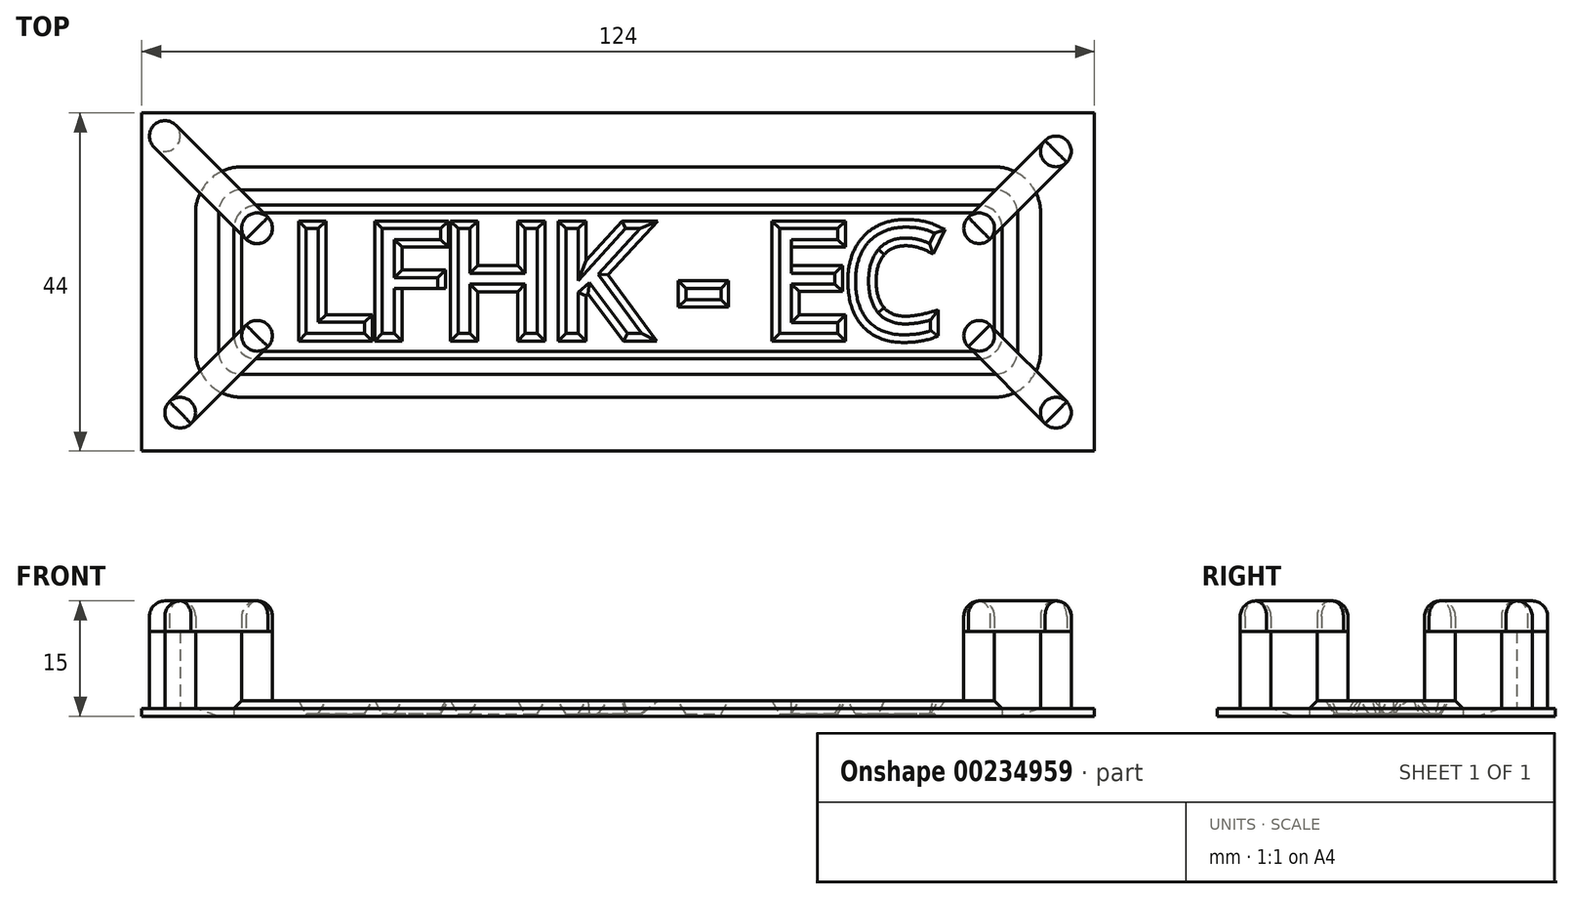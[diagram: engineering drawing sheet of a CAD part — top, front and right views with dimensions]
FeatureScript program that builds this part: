
annotation { "Feature Type Name" : "Feature", "Feature Type Description" : "" }
export const myFeature = defineFeature(function(context is Context, id is Id, definition is map)
    precondition{}
    {
        {
            var Q0;
            Q0=qCreatedBy(makeId("Top.planeOp"),FACE);
            var sketch = newSketch(context, id + "F0", { "sketchPlane" : qUnion([Q0])});
            skLineSegment(sketch, "E0", {"start": v(-50, 3) * mm, "end": v(-50, 17) * mm});
            skLineSegment(sketch, "E1", {"start": v(-47, 20) * mm, "end": v(47, 20) * mm});
            skLineSegment(sketch, "E2", {"start": v(50, 17) * mm, "end": v(50, 3) * mm});
            skLineSegment(sketch, "E3", {"start": v(47, 0) * mm, "end": v(-47, 0) * mm});
            skText(sketch, "E4", { "text": "LFHK - EC", "fontName": "OpenSans-Regular.ttf"});
            skPoint(sketch, "E5.visualSharp", {"position": v(-50, 20) * mm});
            skArc(sketch, "E5.filletArc", {"start": v(-47, 20) * mm, "mid": v(-49.12, 19.12) * mm, "end": v(-50, 17) * mm});
            skPoint(sketch, "E6.visualSharp", {"position": v(-50, 0) * mm});
            skArc(sketch, "E6.filletArc", {"start": v(-50, 3) * mm, "mid": v(-49.12, 0.88) * mm, "end": v(-47, 0) * mm});
            skPoint(sketch, "E7.visualSharp", {"position": v(50, 0) * mm});
            skArc(sketch, "E7.filletArc", {"start": v(47, 0) * mm, "mid": v(49.12, 0.88) * mm, "end": v(50, 3) * mm});
            skPoint(sketch, "E8.visualSharp", {"position": v(50, 20) * mm});
            skArc(sketch, "E8.filletArc", {"start": v(50, 17) * mm, "mid": v(49.12, 19.12) * mm, "end": v(47, 20) * mm});
            const initialGuessF0  = {"E4": [-0.04247, 0.00333, 1, 0, 0.01374]};
            skSetInitialGuess(sketch, initialGuessF0);
            skSolve(sketch);
        }
        {
            var Q0;
            Q0=makeQuery(id+"F0.imprint","IMPRINT",FACE,{"disambiguationData":[TD([[makeQuery(id+"F0.imprint","IMPRINT",EDGE,{"derivedFrom":sQuery(id+"F0.wireOp",EDGE,"E0")}),-1.0]])]});
            extrude(context, id + "F1", {"entities" : qUnion([Q0]), "depth" : 2 * mm});
        }
        {
            var Q0;
            Q0=makeQuery(id+"F1.opExtrude","CAP_EDGE",EDGE,{"disambiguationData":[OSD([sQuery(id+"F0.wireOp",EDGE,"E3")])],"isStart":false});
            var Q1;
            Q1=makeQuery(id+"F1.opExtrude","CAP_EDGE",EDGE,{"disambiguationData":[OSD([sQuery(id+"F0.wireOp",EDGE,"E0")])],"isStart":false});
            var Q2;
            Q2=makeQuery(id+"F1.opExtrude","CAP_EDGE",EDGE,{"disambiguationData":[OSD([sQuery(id+"F0.wireOp",EDGE,"E1")])],"isStart":false});
            var Q3;
            Q3=makeQuery(id+"F1.opExtrude","CAP_EDGE",EDGE,{"disambiguationData":[OSD([sQuery(id+"F0.wireOp",EDGE,"E2")])],"isStart":false});
            chamfer(context, id + "F2", {"entities" : qUnion([Q0, Q1, Q2, Q3]), "chamferType" : ChamferType.OFFSET_ANGLE, "width" : 1 * mm, "oppositeDirection" : false, "angle" : 45 * degree, "tangentPropagation" : true});
        }
        {
            var Q0;
            Q0=makeQuery(id+"F1.opExtrude","CAP_EDGE",EDGE,{"disambiguationData":[OSD([sQuery(id+"F0.wireOp",EDGE,"E4.sketch_text.stroke-1")])],"isStart":false});
            var Q1;
            Q1=makeQuery(id+"F1.opExtrude","CAP_EDGE",EDGE,{"disambiguationData":[OSD([sQuery(id+"F0.wireOp",EDGE,"E4.sketch_text.stroke-3")])],"isStart":false});
            var Q2;
            Q2=makeQuery(id+"F1.opExtrude","CAP_EDGE",EDGE,{"disambiguationData":[OSD([sQuery(id+"F0.wireOp",EDGE,"E4.sketch_text.stroke-2")])],"isStart":false});
            var Q3;
            Q3=makeQuery(id+"F1.opExtrude","CAP_EDGE",EDGE,{"disambiguationData":[OSD([sQuery(id+"F0.wireOp",EDGE,"E4.sketch_text.stroke-0")])],"isStart":false});
            var Q4;
            Q4=makeQuery(id+"F1.opExtrude","CAP_EDGE",EDGE,{"disambiguationData":[OSD([sQuery(id+"F0.wireOp",EDGE,"E4.sketch_text.stroke-5")])],"isStart":false});
            var Q5;
            Q5=makeQuery(id+"F1.opExtrude","CAP_EDGE",EDGE,{"disambiguationData":[OSD([sQuery(id+"F0.wireOp",EDGE,"E4.sketch_text.stroke-4")])],"isStart":false});
            var Q6;
            Q6=makeQuery(id+"F1.opExtrude","CAP_EDGE",EDGE,{"disambiguationData":[OSD([sQuery(id+"F0.wireOp",EDGE,"E4.sketch_text.stroke-13")])],"isStart":false});
            var Q7;
            Q7=makeQuery(id+"F1.opExtrude","CAP_EDGE",EDGE,{"disambiguationData":[OSD([sQuery(id+"F0.wireOp",EDGE,"E4.sketch_text.stroke-9")])],"isStart":false});
            var Q8;
            Q8=makeQuery(id+"F1.opExtrude","CAP_EDGE",EDGE,{"disambiguationData":[OSD([sQuery(id+"F0.wireOp",EDGE,"E4.sketch_text.stroke-8")])],"isStart":false});
            var Q9;
            Q9=makeQuery(id+"F1.opExtrude","CAP_EDGE",EDGE,{"disambiguationData":[OSD([sQuery(id+"F0.wireOp",EDGE,"E4.sketch_text.stroke-10")])],"isStart":false});
            var Q10;
            Q10=makeQuery(id+"F1.opExtrude","CAP_EDGE",EDGE,{"disambiguationData":[OSD([sQuery(id+"F0.wireOp",EDGE,"E4.sketch_text.stroke-12")])],"isStart":false});
            var Q11;
            Q11=makeQuery(id+"F1.opExtrude","CAP_EDGE",EDGE,{"disambiguationData":[OSD([sQuery(id+"F0.wireOp",EDGE,"E4.sketch_text.stroke-11")])],"isStart":false});
            var Q12;
            Q12=makeQuery(id+"F1.opExtrude","CAP_EDGE",EDGE,{"disambiguationData":[OSD([sQuery(id+"F0.wireOp",EDGE,"E4.sketch_text.stroke-7")])],"isStart":false});
            var Q13;
            Q13=makeQuery(id+"F1.opExtrude","CAP_EDGE",EDGE,{"disambiguationData":[OSD([sQuery(id+"F0.wireOp",EDGE,"E4.sketch_text.stroke-15")])],"isStart":false});
            var Q14;
            Q14=makeQuery(id+"F1.opExtrude","CAP_EDGE",EDGE,{"disambiguationData":[OSD([sQuery(id+"F0.wireOp",EDGE,"E4.sketch_text.stroke-6")])],"isStart":false});
            var Q15;
            Q15=makeQuery(id+"F1.opExtrude","CAP_EDGE",EDGE,{"disambiguationData":[OSD([sQuery(id+"F0.wireOp",EDGE,"E4.sketch_text.stroke-21")])],"isStart":false});
            var Q16;
            Q16=makeQuery(id+"F1.opExtrude","CAP_EDGE",EDGE,{"disambiguationData":[OSD([sQuery(id+"F0.wireOp",EDGE,"E4.sketch_text.stroke-22")])],"isStart":false});
            var Q17;
            Q17=makeQuery(id+"F1.opExtrude","CAP_EDGE",EDGE,{"disambiguationData":[OSD([sQuery(id+"F0.wireOp",EDGE,"E4.sketch_text.stroke-23")])],"isStart":false});
            var Q18;
            Q18=makeQuery(id+"F1.opExtrude","CAP_EDGE",EDGE,{"disambiguationData":[OSD([sQuery(id+"F0.wireOp",EDGE,"E4.sketch_text.stroke-26")])],"isStart":false});
            var Q19;
            Q19=makeQuery(id+"F1.opExtrude","CAP_EDGE",EDGE,{"disambiguationData":[OSD([sQuery(id+"F0.wireOp",EDGE,"E4.sketch_text.stroke-25")])],"isStart":false});
            var Q20;
            Q20=makeQuery(id+"F1.opExtrude","CAP_EDGE",EDGE,{"disambiguationData":[OSD([sQuery(id+"F0.wireOp",EDGE,"E4.sketch_text.stroke-24")])],"isStart":false});
            var Q21;
            Q21=makeQuery(id+"F1.opExtrude","CAP_EDGE",EDGE,{"disambiguationData":[OSD([sQuery(id+"F0.wireOp",EDGE,"E4.sketch_text.stroke-18")])],"isStart":false});
            var Q22;
            Q22=makeQuery(id+"F1.opExtrude","CAP_EDGE",EDGE,{"disambiguationData":[OSD([sQuery(id+"F0.wireOp",EDGE,"E4.sketch_text.stroke-19")])],"isStart":false});
            var Q23;
            Q23=makeQuery(id+"F1.opExtrude","CAP_EDGE",EDGE,{"disambiguationData":[OSD([sQuery(id+"F0.wireOp",EDGE,"E4.sketch_text.stroke-20")])],"isStart":false});
            var Q24;
            Q24=makeQuery(id+"F1.opExtrude","CAP_EDGE",EDGE,{"disambiguationData":[OSD([sQuery(id+"F0.wireOp",EDGE,"E4.sketch_text.stroke-16")])],"isStart":false});
            var Q25;
            Q25=makeQuery(id+"F1.opExtrude","CAP_EDGE",EDGE,{"disambiguationData":[OSD([sQuery(id+"F0.wireOp",EDGE,"E4.sketch_text.stroke-17")])],"isStart":false});
            var Q26;
            Q26=makeQuery(id+"F1.opExtrude","CAP_EDGE",EDGE,{"disambiguationData":[OSD([sQuery(id+"F0.wireOp",EDGE,"E4.sketch_text.stroke-27")])],"isStart":false});
            var Q27;
            Q27=makeQuery(id+"F1.opExtrude","CAP_EDGE",EDGE,{"disambiguationData":[OSD([sQuery(id+"F0.wireOp",EDGE,"E4.sketch_text.stroke-33")])],"isStart":false});
            var Q28;
            Q28=makeQuery(id+"F1.opExtrude","CAP_EDGE",EDGE,{"disambiguationData":[OSD([sQuery(id+"F0.wireOp",EDGE,"E4.sketch_text.stroke-34")])],"isStart":false});
            var Q29;
            Q29=makeQuery(id+"F1.opExtrude","CAP_EDGE",EDGE,{"disambiguationData":[OSD([sQuery(id+"F0.wireOp",EDGE,"E4.sketch_text.stroke-35")])],"isStart":false});
            var Q30;
            Q30=makeQuery(id+"F1.opExtrude","CAP_EDGE",EDGE,{"disambiguationData":[OSD([sQuery(id+"F0.wireOp",EDGE,"E4.sketch_text.stroke-30")])],"isStart":false});
            var Q31;
            Q31=makeQuery(id+"F1.opExtrude","CAP_EDGE",EDGE,{"disambiguationData":[OSD([sQuery(id+"F0.wireOp",EDGE,"E4.sketch_text.stroke-36")])],"isStart":false});
            var Q32;
            Q32=makeQuery(id+"F1.opExtrude","CAP_EDGE",EDGE,{"disambiguationData":[OSD([sQuery(id+"F0.wireOp",EDGE,"E4.sketch_text.stroke-31")])],"isStart":false});
            var Q33;
            Q33=makeQuery(id+"F1.opExtrude","CAP_EDGE",EDGE,{"disambiguationData":[OSD([sQuery(id+"F0.wireOp",EDGE,"E4.sketch_text.stroke-32")])],"isStart":false});
            var Q34;
            Q34=makeQuery(id+"F1.opExtrude","CAP_EDGE",EDGE,{"disambiguationData":[OSD([sQuery(id+"F0.wireOp",EDGE,"E4.sketch_text.stroke-37")])],"isStart":false});
            var Q35;
            Q35=makeQuery(id+"F1.opExtrude","CAP_EDGE",EDGE,{"disambiguationData":[OSD([sQuery(id+"F0.wireOp",EDGE,"E4.sketch_text.stroke-38")])],"isStart":false});
            var Q36;
            Q36=makeQuery(id+"F1.opExtrude","CAP_EDGE",EDGE,{"disambiguationData":[OSD([sQuery(id+"F0.wireOp",EDGE,"E4.sketch_text.stroke-39")])],"isStart":false});
            var Q37;
            Q37=makeQuery(id+"F1.opExtrude","CAP_EDGE",EDGE,{"disambiguationData":[OSD([sQuery(id+"F0.wireOp",EDGE,"E4.sketch_text.stroke-29")])],"isStart":false});
            var Q38;
            Q38=makeQuery(id+"F1.opExtrude","CAP_EDGE",EDGE,{"disambiguationData":[OSD([sQuery(id+"F0.wireOp",EDGE,"E4.sketch_text.stroke-28")])],"isStart":false});
            var Q39;
            Q39=makeQuery(id+"F1.opExtrude","CAP_EDGE",EDGE,{"disambiguationData":[OSD([sQuery(id+"F0.wireOp",EDGE,"E4.sketch_text.stroke-41")])],"isStart":false});
            var Q40;
            Q40=makeQuery(id+"F1.opExtrude","CAP_EDGE",EDGE,{"disambiguationData":[OSD([sQuery(id+"F0.wireOp",EDGE,"E4.sketch_text.stroke-42")])],"isStart":false});
            var Q41;
            Q41=makeQuery(id+"F1.opExtrude","CAP_EDGE",EDGE,{"disambiguationData":[OSD([sQuery(id+"F0.wireOp",EDGE,"E4.sketch_text.stroke-43")])],"isStart":false});
            var Q42;
            Q42=makeQuery(id+"F1.opExtrude","CAP_EDGE",EDGE,{"disambiguationData":[OSD([sQuery(id+"F0.wireOp",EDGE,"E4.sketch_text.stroke-40")])],"isStart":false});
            var Q43;
            Q43=makeQuery(id+"F1.opExtrude","CAP_EDGE",EDGE,{"disambiguationData":[OSD([sQuery(id+"F0.wireOp",EDGE,"E4.sketch_text.stroke-46")])],"isStart":false});
            var Q44;
            Q44=makeQuery(id+"F1.opExtrude","CAP_EDGE",EDGE,{"disambiguationData":[OSD([sQuery(id+"F0.wireOp",EDGE,"E4.sketch_text.stroke-45")])],"isStart":false});
            var Q45;
            Q45=makeQuery(id+"F1.opExtrude","CAP_EDGE",EDGE,{"disambiguationData":[OSD([sQuery(id+"F0.wireOp",EDGE,"E4.sketch_text.stroke-47")])],"isStart":false});
            var Q46;
            Q46=makeQuery(id+"F1.opExtrude","CAP_EDGE",EDGE,{"disambiguationData":[OSD([sQuery(id+"F0.wireOp",EDGE,"E4.sketch_text.stroke-48")])],"isStart":false});
            var Q47;
            Q47=makeQuery(id+"F1.opExtrude","CAP_EDGE",EDGE,{"disambiguationData":[OSD([sQuery(id+"F0.wireOp",EDGE,"E4.sketch_text.stroke-50")])],"isStart":false});
            var Q48;
            Q48=makeQuery(id+"F1.opExtrude","CAP_EDGE",EDGE,{"disambiguationData":[OSD([sQuery(id+"F0.wireOp",EDGE,"E4.sketch_text.stroke-51")])],"isStart":false});
            var Q49;
            Q49=makeQuery(id+"F1.opExtrude","CAP_EDGE",EDGE,{"disambiguationData":[OSD([sQuery(id+"F0.wireOp",EDGE,"E4.sketch_text.stroke-52")])],"isStart":false});
            var Q50;
            Q50=makeQuery(id+"F1.opExtrude","CAP_EDGE",EDGE,{"disambiguationData":[OSD([sQuery(id+"F0.wireOp",EDGE,"E4.sketch_text.stroke-54")])],"isStart":false});
            var Q51;
            Q51=makeQuery(id+"F1.opExtrude","CAP_EDGE",EDGE,{"disambiguationData":[OSD([sQuery(id+"F0.wireOp",EDGE,"E4.sketch_text.stroke-53")])],"isStart":false});
            var Q52;
            Q52=makeQuery(id+"F1.opExtrude","CAP_EDGE",EDGE,{"disambiguationData":[OSD([sQuery(id+"F0.wireOp",EDGE,"E4.sketch_text.stroke-55")])],"isStart":false});
            var Q53;
            Q53=makeQuery(id+"F1.opExtrude","CAP_EDGE",EDGE,{"disambiguationData":[OSD([sQuery(id+"F0.wireOp",EDGE,"E4.sketch_text.stroke-44")])],"isStart":false});
            var Q54;
            Q54=makeQuery(id+"F1.opExtrude","CAP_EDGE",EDGE,{"disambiguationData":[OSD([sQuery(id+"F0.wireOp",EDGE,"E4.sketch_text.stroke-64")])],"isStart":false});
            var Q55;
            Q55=makeQuery(id+"F1.opExtrude","CAP_EDGE",EDGE,{"disambiguationData":[OSD([sQuery(id+"F0.wireOp",EDGE,"E4.sketch_text.stroke-59")])],"isStart":false});
            var Q56;
            Q56=makeQuery(id+"F1.opExtrude","CAP_EDGE",EDGE,{"disambiguationData":[OSD([sQuery(id+"F0.wireOp",EDGE,"E4.sketch_text.stroke-61")])],"isStart":false});
            var Q57;
            Q57=makeQuery(id+"F1.opExtrude","CAP_EDGE",EDGE,{"disambiguationData":[OSD([sQuery(id+"F0.wireOp",EDGE,"E4.sketch_text.stroke-69")])],"isStart":false});
            chamfer(context, id + "F3", {"entities" : qUnion([Q0, Q1, Q2, Q3, Q4, Q5, Q6, Q7, Q8, Q9, Q10, Q11, Q12, Q13, Q14, Q15, Q16, Q17, Q18, Q19, Q20, Q21, Q22, Q23, Q24, Q25, Q26, Q27, Q28, Q29, Q30, Q31, Q32, Q33, Q34, Q35, Q36, Q37, Q38, Q39, Q40, Q41, Q42, Q43, Q44, Q45, Q46, Q47, Q48, Q49, Q50, Q51, Q52, Q53, Q54, Q55, Q56, Q57]), "chamferType" : ChamferType.OFFSET_ANGLE, "width" : 1 * mm, "oppositeDirection" : false, "angle" : 60 * degree, "tangentPropagation" : true});
        }
        {
            var Q0;
            Q0=qCreatedBy(makeId("Top.planeOp"),FACE);
            var sketch = newSketch(context, id + "F4", { "sketchPlane" : qUnion([Q0])});
            skLineSegment(sketch, "E9.bottom", {"start": v(-49, 22) * mm, "end": v(49, 22) * mm});
            skLineSegment(sketch, "E9.top", {"start": v(-49, -2) * mm, "end": v(49, -2) * mm});
            skLineSegment(sketch, "E9.left", {"start": v(-52, 19) * mm, "end": v(-52, 1) * mm});
            skLineSegment(sketch, "E9.right", {"start": v(52, 19) * mm, "end": v(52, 1) * mm});
            skPoint(sketch, "E10.visualSharp", {"position": v(-52, 22) * mm});
            skPoint(sketch, "E11.visualSharp", {"position": v(-52, -2) * mm});
            skPoint(sketch, "E12.visualSharp", {"position": v(52, 22) * mm});
            skArc(sketch, "E13.filletArc", {"start": v(-49, 22) * mm, "mid": v(-51.12, 21.12) * mm, "end": v(-52, 19) * mm});
            skArc(sketch, "E14.filletArc", {"start": v(-52, 1) * mm, "mid": v(-51.12, -1.12) * mm, "end": v(-49, -2) * mm});
            skPoint(sketch, "E15.visualSharp", {"position": v(52, -2) * mm});
            skArc(sketch, "E15.filletArc", {"start": v(49, -2) * mm, "mid": v(51.12, -1.12) * mm, "end": v(52, 1) * mm});
            skArc(sketch, "E16.filletArc", {"start": v(52, 19) * mm, "mid": v(51.12, 21.12) * mm, "end": v(49, 22) * mm});
            skLineSegment(sketch, "E17.bottom", {"start": v(-62, 32) * mm, "end": v(62, 32) * mm});
            skLineSegment(sketch, "E17.top", {"start": v(-62, -12) * mm, "end": v(62, -12) * mm});
            skLineSegment(sketch, "E17.left", {"start": v(-62, 32) * mm, "end": v(-62, -12) * mm});
            skLineSegment(sketch, "E17.right", {"start": v(62, 32) * mm, "end": v(62, -12) * mm});
            skSolve(sketch);
        }
        {
            var Q0;
            Q0=makeQuery(id+"F4.imprint","IMPRINT",FACE,{"disambiguationData":[TD([[makeQuery(id+"F4.imprint","IMPRINT",EDGE,{"derivedFrom":sQuery(id+"F4.wireOp",EDGE,"E9.bottom")}),1.0]])]});
            extrude(context, id + "F5", {"entities" : qUnion([Q0]), "depth" : 1 * mm});
        }
        {
            var Q0;
            Q0=makeQuery(id+"F5.opExtrude","CAP_EDGE",EDGE,{"disambiguationData":[OSD([sQuery(id+"F4.wireOp",EDGE,"E9.bottom")])],"isStart":false});
            chamfer(context, id + "F6", {"entities" : qUnion([Q0]), "chamferType" : ChamferType.TWO_OFFSETS, "width1" : 3 * mm, "oppositeDirection" : false, "width2" : 1 * mm, "tangentPropagation" : true});
        }
        {
            var Q0;
            Q0=makeQuery(id+"F1.opExtrude","CAP_FACE",FACE,{"disambiguationData":[OSD([sQuery(id+"F0.wireOp",EDGE,"E0"),sQuery(id+"F0.wireOp",EDGE,"E1"),sQuery(id+"F0.wireOp",EDGE,"E2"),sQuery(id+"F0.wireOp",EDGE,"E3"),sQuery(id+"F0.wireOp",EDGE,"E4.sketch_text.stroke-0"),sQuery(id+"F0.wireOp",EDGE,"E4.sketch_text.stroke-1"),sQuery(id+"F0.wireOp",EDGE,"E4.sketch_text.stroke-2"),sQuery(id+"F0.wireOp",EDGE,"E4.sketch_text.stroke-3"),sQuery(id+"F0.wireOp",EDGE,"E4.sketch_text.stroke-4"),sQuery(id+"F0.wireOp",EDGE,"E4.sketch_text.stroke-5"),sQuery(id+"F0.wireOp",EDGE,"E4.sketch_text.stroke-6"),sQuery(id+"F0.wireOp",EDGE,"E4.sketch_text.stroke-7"),sQuery(id+"F0.wireOp",EDGE,"E4.sketch_text.stroke-8"),sQuery(id+"F0.wireOp",EDGE,"E4.sketch_text.stroke-9"),sQuery(id+"F0.wireOp",EDGE,"E4.sketch_text.stroke-10"),sQuery(id+"F0.wireOp",EDGE,"E4.sketch_text.stroke-11"),sQuery(id+"F0.wireOp",EDGE,"E4.sketch_text.stroke-12"),sQuery(id+"F0.wireOp",EDGE,"E4.sketch_text.stroke-13"),sQuery(id+"F0.wireOp",EDGE,"E4.sketch_text.stroke-14"),sQuery(id+"F0.wireOp",EDGE,"E4.sketch_text.stroke-15"),sQuery(id+"F0.wireOp",EDGE,"E4.sketch_text.stroke-16"),sQuery(id+"F0.wireOp",EDGE,"E4.sketch_text.stroke-17"),sQuery(id+"F0.wireOp",EDGE,"E4.sketch_text.stroke-18"),sQuery(id+"F0.wireOp",EDGE,"E4.sketch_text.stroke-19"),sQuery(id+"F0.wireOp",EDGE,"E4.sketch_text.stroke-20"),sQuery(id+"F0.wireOp",EDGE,"E4.sketch_text.stroke-21"),sQuery(id+"F0.wireOp",EDGE,"E4.sketch_text.stroke-22"),sQuery(id+"F0.wireOp",EDGE,"E4.sketch_text.stroke-23"),sQuery(id+"F0.wireOp",EDGE,"E4.sketch_text.stroke-24"),sQuery(id+"F0.wireOp",EDGE,"E4.sketch_text.stroke-25"),sQuery(id+"F0.wireOp",EDGE,"E4.sketch_text.stroke-26"),sQuery(id+"F0.wireOp",EDGE,"E4.sketch_text.stroke-27"),sQuery(id+"F0.wireOp",EDGE,"E4.sketch_text.stroke-28"),sQuery(id+"F0.wireOp",EDGE,"E4.sketch_text.stroke-29"),sQuery(id+"F0.wireOp",EDGE,"E4.sketch_text.stroke-30"),sQuery(id+"F0.wireOp",EDGE,"E4.sketch_text.stroke-31"),sQuery(id+"F0.wireOp",EDGE,"E4.sketch_text.stroke-32"),sQuery(id+"F0.wireOp",EDGE,"E4.sketch_text.stroke-33"),sQuery(id+"F0.wireOp",EDGE,"E4.sketch_text.stroke-34"),sQuery(id+"F0.wireOp",EDGE,"E4.sketch_text.stroke-35"),sQuery(id+"F0.wireOp",EDGE,"E4.sketch_text.stroke-36"),sQuery(id+"F0.wireOp",EDGE,"E4.sketch_text.stroke-37"),sQuery(id+"F0.wireOp",EDGE,"E4.sketch_text.stroke-38"),sQuery(id+"F0.wireOp",EDGE,"E4.sketch_text.stroke-39"),sQuery(id+"F0.wireOp",EDGE,"E4.sketch_text.stroke-40"),sQuery(id+"F0.wireOp",EDGE,"E4.sketch_text.stroke-41"),sQuery(id+"F0.wireOp",EDGE,"E4.sketch_text.stroke-42"),sQuery(id+"F0.wireOp",EDGE,"E4.sketch_text.stroke-43"),sQuery(id+"F0.wireOp",EDGE,"E4.sketch_text.stroke-44"),sQuery(id+"F0.wireOp",EDGE,"E4.sketch_text.stroke-45"),sQuery(id+"F0.wireOp",EDGE,"E4.sketch_text.stroke-46"),sQuery(id+"F0.wireOp",EDGE,"E4.sketch_text.stroke-47"),sQuery(id+"F0.wireOp",EDGE,"E4.sketch_text.stroke-48"),sQuery(id+"F0.wireOp",EDGE,"E4.sketch_text.stroke-49"),sQuery(id+"F0.wireOp",EDGE,"E4.sketch_text.stroke-50"),sQuery(id+"F0.wireOp",EDGE,"E4.sketch_text.stroke-51"),sQuery(id+"F0.wireOp",EDGE,"E4.sketch_text.stroke-52"),sQuery(id+"F0.wireOp",EDGE,"E4.sketch_text.stroke-53"),sQuery(id+"F0.wireOp",EDGE,"E4.sketch_text.stroke-54"),sQuery(id+"F0.wireOp",EDGE,"E4.sketch_text.stroke-55"),sQuery(id+"F0.wireOp",EDGE,"E4.sketch_text.stroke-56"),sQuery(id+"F0.wireOp",EDGE,"E4.sketch_text.stroke-57"),sQuery(id+"F0.wireOp",EDGE,"E4.sketch_text.stroke-58"),sQuery(id+"F0.wireOp",EDGE,"E4.sketch_text.stroke-59"),sQuery(id+"F0.wireOp",EDGE,"E4.sketch_text.stroke-60"),sQuery(id+"F0.wireOp",EDGE,"E4.sketch_text.stroke-61"),sQuery(id+"F0.wireOp",EDGE,"E4.sketch_text.stroke-62"),sQuery(id+"F0.wireOp",EDGE,"E4.sketch_text.stroke-63"),sQuery(id+"F0.wireOp",EDGE,"E4.sketch_text.stroke-64"),sQuery(id+"F0.wireOp",EDGE,"E4.sketch_text.stroke-65"),sQuery(id+"F0.wireOp",EDGE,"E4.sketch_text.stroke-66"),sQuery(id+"F0.wireOp",EDGE,"E4.sketch_text.stroke-67"),sQuery(id+"F0.wireOp",EDGE,"E4.sketch_text.stroke-68"),sQuery(id+"F0.wireOp",EDGE,"E4.sketch_text.stroke-69"),sQuery(id+"F0.wireOp",EDGE,"E4.sketch_text.stroke-70"),sQuery(id+"F0.wireOp",EDGE,"E5.filletArc"),sQuery(id+"F0.wireOp",EDGE,"E6.filletArc"),sQuery(id+"F0.wireOp",EDGE,"E7.filletArc"),sQuery(id+"F0.wireOp",EDGE,"E8.filletArc")])],"isStart":false});
            var sketch = newSketch(context, id + "F7", { "sketchPlane" : qUnion([Q0])});
            skCircle(sketch, "E18", {"center": v(47, 17) * mm, "radius": 2 * mm});
            skCircle(sketch, "E19", {"center": v(47, 3) * mm, "radius": 2 * mm});
            skCircle(sketch, "E20", {"center": v(-47, 17) * mm, "radius": 2 * mm});
            skCircle(sketch, "E21", {"center": v(-47, 3) * mm, "radius": 2 * mm});
            skSolve(sketch);
        }
        {
            var Q0;
            {var subQ0=sQuery(id+"F7.wireOp",EDGE,"E20");var subQ1=sQuery(id+"F0.wireOp",EDGE,"E1");var subQ2=sQuery(id+"F0.wireOp",EDGE,"E0");var subQ3=makeQuery(id+"F1.opExtrude","CAP_FACE",FACE,{"disambiguationData":[OSD([subQ2,subQ1,sQuery(id+"F0.wireOp",EDGE,"E2"),sQuery(id+"F0.wireOp",EDGE,"E3"),sQuery(id+"F0.wireOp",EDGE,"E4.sketch_text.stroke-0"),sQuery(id+"F0.wireOp",EDGE,"E4.sketch_text.stroke-1"),sQuery(id+"F0.wireOp",EDGE,"E4.sketch_text.stroke-2"),sQuery(id+"F0.wireOp",EDGE,"E4.sketch_text.stroke-3"),sQuery(id+"F0.wireOp",EDGE,"E4.sketch_text.stroke-4"),sQuery(id+"F0.wireOp",EDGE,"E4.sketch_text.stroke-5"),sQuery(id+"F0.wireOp",EDGE,"E4.sketch_text.stroke-6"),sQuery(id+"F0.wireOp",EDGE,"E4.sketch_text.stroke-7"),sQuery(id+"F0.wireOp",EDGE,"E4.sketch_text.stroke-8"),sQuery(id+"F0.wireOp",EDGE,"E4.sketch_text.stroke-9"),sQuery(id+"F0.wireOp",EDGE,"E4.sketch_text.stroke-10"),sQuery(id+"F0.wireOp",EDGE,"E4.sketch_text.stroke-11"),sQuery(id+"F0.wireOp",EDGE,"E4.sketch_text.stroke-12"),sQuery(id+"F0.wireOp",EDGE,"E4.sketch_text.stroke-13"),sQuery(id+"F0.wireOp",EDGE,"E4.sketch_text.stroke-14"),sQuery(id+"F0.wireOp",EDGE,"E4.sketch_text.stroke-15"),sQuery(id+"F0.wireOp",EDGE,"E4.sketch_text.stroke-16"),sQuery(id+"F0.wireOp",EDGE,"E4.sketch_text.stroke-17"),sQuery(id+"F0.wireOp",EDGE,"E4.sketch_text.stroke-18"),sQuery(id+"F0.wireOp",EDGE,"E4.sketch_text.stroke-19"),sQuery(id+"F0.wireOp",EDGE,"E4.sketch_text.stroke-20"),sQuery(id+"F0.wireOp",EDGE,"E4.sketch_text.stroke-21"),sQuery(id+"F0.wireOp",EDGE,"E4.sketch_text.stroke-22"),sQuery(id+"F0.wireOp",EDGE,"E4.sketch_text.stroke-23"),sQuery(id+"F0.wireOp",EDGE,"E4.sketch_text.stroke-24"),sQuery(id+"F0.wireOp",EDGE,"E4.sketch_text.stroke-25"),sQuery(id+"F0.wireOp",EDGE,"E4.sketch_text.stroke-26"),sQuery(id+"F0.wireOp",EDGE,"E4.sketch_text.stroke-27"),sQuery(id+"F0.wireOp",EDGE,"E4.sketch_text.stroke-28"),sQuery(id+"F0.wireOp",EDGE,"E4.sketch_text.stroke-29"),sQuery(id+"F0.wireOp",EDGE,"E4.sketch_text.stroke-30"),sQuery(id+"F0.wireOp",EDGE,"E4.sketch_text.stroke-31"),sQuery(id+"F0.wireOp",EDGE,"E4.sketch_text.stroke-32"),sQuery(id+"F0.wireOp",EDGE,"E4.sketch_text.stroke-33"),sQuery(id+"F0.wireOp",EDGE,"E4.sketch_text.stroke-34"),sQuery(id+"F0.wireOp",EDGE,"E4.sketch_text.stroke-35"),sQuery(id+"F0.wireOp",EDGE,"E4.sketch_text.stroke-36"),sQuery(id+"F0.wireOp",EDGE,"E4.sketch_text.stroke-37"),sQuery(id+"F0.wireOp",EDGE,"E4.sketch_text.stroke-38"),sQuery(id+"F0.wireOp",EDGE,"E4.sketch_text.stroke-39"),sQuery(id+"F0.wireOp",EDGE,"E4.sketch_text.stroke-40"),sQuery(id+"F0.wireOp",EDGE,"E4.sketch_text.stroke-41"),sQuery(id+"F0.wireOp",EDGE,"E4.sketch_text.stroke-42"),sQuery(id+"F0.wireOp",EDGE,"E4.sketch_text.stroke-43"),sQuery(id+"F0.wireOp",EDGE,"E4.sketch_text.stroke-44"),sQuery(id+"F0.wireOp",EDGE,"E4.sketch_text.stroke-45"),sQuery(id+"F0.wireOp",EDGE,"E4.sketch_text.stroke-46"),sQuery(id+"F0.wireOp",EDGE,"E4.sketch_text.stroke-47"),sQuery(id+"F0.wireOp",EDGE,"E4.sketch_text.stroke-48"),sQuery(id+"F0.wireOp",EDGE,"E4.sketch_text.stroke-49"),sQuery(id+"F0.wireOp",EDGE,"E4.sketch_text.stroke-50"),sQuery(id+"F0.wireOp",EDGE,"E4.sketch_text.stroke-51"),sQuery(id+"F0.wireOp",EDGE,"E4.sketch_text.stroke-52"),sQuery(id+"F0.wireOp",EDGE,"E4.sketch_text.stroke-53"),sQuery(id+"F0.wireOp",EDGE,"E4.sketch_text.stroke-54"),sQuery(id+"F0.wireOp",EDGE,"E4.sketch_text.stroke-55"),sQuery(id+"F0.wireOp",EDGE,"E4.sketch_text.stroke-56"),sQuery(id+"F0.wireOp",EDGE,"E4.sketch_text.stroke-57"),sQuery(id+"F0.wireOp",EDGE,"E4.sketch_text.stroke-58"),sQuery(id+"F0.wireOp",EDGE,"E4.sketch_text.stroke-59"),sQuery(id+"F0.wireOp",EDGE,"E4.sketch_text.stroke-60"),sQuery(id+"F0.wireOp",EDGE,"E4.sketch_text.stroke-61"),sQuery(id+"F0.wireOp",EDGE,"E4.sketch_text.stroke-62"),sQuery(id+"F0.wireOp",EDGE,"E4.sketch_text.stroke-63"),sQuery(id+"F0.wireOp",EDGE,"E4.sketch_text.stroke-64"),sQuery(id+"F0.wireOp",EDGE,"E4.sketch_text.stroke-65"),sQuery(id+"F0.wireOp",EDGE,"E4.sketch_text.stroke-66"),sQuery(id+"F0.wireOp",EDGE,"E4.sketch_text.stroke-67"),sQuery(id+"F0.wireOp",EDGE,"E4.sketch_text.stroke-68"),sQuery(id+"F0.wireOp",EDGE,"E4.sketch_text.stroke-69"),sQuery(id+"F0.wireOp",EDGE,"E4.sketch_text.stroke-70"),sQuery(id+"F0.wireOp",EDGE,"E5.filletArc"),sQuery(id+"F0.wireOp",EDGE,"E6.filletArc"),sQuery(id+"F0.wireOp",EDGE,"E7.filletArc"),sQuery(id+"F0.wireOp",EDGE,"E8.filletArc")])],"isStart":false});var subQ4=makeQuery(id+"F7.imprint","INTERSECT",VERTEX,{"derivedFrom":[makeQuery(id+"F2.opChamfer","BLEND_EDGE",EDGE,{"blendedFrom":[makeQuery(id+"F1.opExtrude","CAP_EDGE",EDGE,{"disambiguationData":[OSD([subQ2])],"isStart":false}),subQ3],"blendedInto":[subQ3]}),subQ0]});Q0=makeQuery(id+"F7.imprint","IMPRINT",FACE,{"disambiguationData":[TD([[makeQuery(id+"F7.imprint","IMPRINT",EDGE,{"disambiguationData":[TD([[subQ4,1.0]])],"derivedFrom":subQ0}),1.0]])]});}
            var Q1;
            {var subQ0=sQuery(id+"F7.wireOp",EDGE,"E21");var subQ1=sQuery(id+"F0.wireOp",EDGE,"E3");var subQ2=sQuery(id+"F0.wireOp",EDGE,"E0");var subQ3=makeQuery(id+"F1.opExtrude","CAP_FACE",FACE,{"disambiguationData":[OSD([subQ2,sQuery(id+"F0.wireOp",EDGE,"E1"),sQuery(id+"F0.wireOp",EDGE,"E2"),subQ1,sQuery(id+"F0.wireOp",EDGE,"E4.sketch_text.stroke-0"),sQuery(id+"F0.wireOp",EDGE,"E4.sketch_text.stroke-1"),sQuery(id+"F0.wireOp",EDGE,"E4.sketch_text.stroke-2"),sQuery(id+"F0.wireOp",EDGE,"E4.sketch_text.stroke-3"),sQuery(id+"F0.wireOp",EDGE,"E4.sketch_text.stroke-4"),sQuery(id+"F0.wireOp",EDGE,"E4.sketch_text.stroke-5"),sQuery(id+"F0.wireOp",EDGE,"E4.sketch_text.stroke-6"),sQuery(id+"F0.wireOp",EDGE,"E4.sketch_text.stroke-7"),sQuery(id+"F0.wireOp",EDGE,"E4.sketch_text.stroke-8"),sQuery(id+"F0.wireOp",EDGE,"E4.sketch_text.stroke-9"),sQuery(id+"F0.wireOp",EDGE,"E4.sketch_text.stroke-10"),sQuery(id+"F0.wireOp",EDGE,"E4.sketch_text.stroke-11"),sQuery(id+"F0.wireOp",EDGE,"E4.sketch_text.stroke-12"),sQuery(id+"F0.wireOp",EDGE,"E4.sketch_text.stroke-13"),sQuery(id+"F0.wireOp",EDGE,"E4.sketch_text.stroke-14"),sQuery(id+"F0.wireOp",EDGE,"E4.sketch_text.stroke-15"),sQuery(id+"F0.wireOp",EDGE,"E4.sketch_text.stroke-16"),sQuery(id+"F0.wireOp",EDGE,"E4.sketch_text.stroke-17"),sQuery(id+"F0.wireOp",EDGE,"E4.sketch_text.stroke-18"),sQuery(id+"F0.wireOp",EDGE,"E4.sketch_text.stroke-19"),sQuery(id+"F0.wireOp",EDGE,"E4.sketch_text.stroke-20"),sQuery(id+"F0.wireOp",EDGE,"E4.sketch_text.stroke-21"),sQuery(id+"F0.wireOp",EDGE,"E4.sketch_text.stroke-22"),sQuery(id+"F0.wireOp",EDGE,"E4.sketch_text.stroke-23"),sQuery(id+"F0.wireOp",EDGE,"E4.sketch_text.stroke-24"),sQuery(id+"F0.wireOp",EDGE,"E4.sketch_text.stroke-25"),sQuery(id+"F0.wireOp",EDGE,"E4.sketch_text.stroke-26"),sQuery(id+"F0.wireOp",EDGE,"E4.sketch_text.stroke-27"),sQuery(id+"F0.wireOp",EDGE,"E4.sketch_text.stroke-28"),sQuery(id+"F0.wireOp",EDGE,"E4.sketch_text.stroke-29"),sQuery(id+"F0.wireOp",EDGE,"E4.sketch_text.stroke-30"),sQuery(id+"F0.wireOp",EDGE,"E4.sketch_text.stroke-31"),sQuery(id+"F0.wireOp",EDGE,"E4.sketch_text.stroke-32"),sQuery(id+"F0.wireOp",EDGE,"E4.sketch_text.stroke-33"),sQuery(id+"F0.wireOp",EDGE,"E4.sketch_text.stroke-34"),sQuery(id+"F0.wireOp",EDGE,"E4.sketch_text.stroke-35"),sQuery(id+"F0.wireOp",EDGE,"E4.sketch_text.stroke-36"),sQuery(id+"F0.wireOp",EDGE,"E4.sketch_text.stroke-37"),sQuery(id+"F0.wireOp",EDGE,"E4.sketch_text.stroke-38"),sQuery(id+"F0.wireOp",EDGE,"E4.sketch_text.stroke-39"),sQuery(id+"F0.wireOp",EDGE,"E4.sketch_text.stroke-40"),sQuery(id+"F0.wireOp",EDGE,"E4.sketch_text.stroke-41"),sQuery(id+"F0.wireOp",EDGE,"E4.sketch_text.stroke-42"),sQuery(id+"F0.wireOp",EDGE,"E4.sketch_text.stroke-43"),sQuery(id+"F0.wireOp",EDGE,"E4.sketch_text.stroke-44"),sQuery(id+"F0.wireOp",EDGE,"E4.sketch_text.stroke-45"),sQuery(id+"F0.wireOp",EDGE,"E4.sketch_text.stroke-46"),sQuery(id+"F0.wireOp",EDGE,"E4.sketch_text.stroke-47"),sQuery(id+"F0.wireOp",EDGE,"E4.sketch_text.stroke-48"),sQuery(id+"F0.wireOp",EDGE,"E4.sketch_text.stroke-49"),sQuery(id+"F0.wireOp",EDGE,"E4.sketch_text.stroke-50"),sQuery(id+"F0.wireOp",EDGE,"E4.sketch_text.stroke-51"),sQuery(id+"F0.wireOp",EDGE,"E4.sketch_text.stroke-52"),sQuery(id+"F0.wireOp",EDGE,"E4.sketch_text.stroke-53"),sQuery(id+"F0.wireOp",EDGE,"E4.sketch_text.stroke-54"),sQuery(id+"F0.wireOp",EDGE,"E4.sketch_text.stroke-55"),sQuery(id+"F0.wireOp",EDGE,"E4.sketch_text.stroke-56"),sQuery(id+"F0.wireOp",EDGE,"E4.sketch_text.stroke-57"),sQuery(id+"F0.wireOp",EDGE,"E4.sketch_text.stroke-58"),sQuery(id+"F0.wireOp",EDGE,"E4.sketch_text.stroke-59"),sQuery(id+"F0.wireOp",EDGE,"E4.sketch_text.stroke-60"),sQuery(id+"F0.wireOp",EDGE,"E4.sketch_text.stroke-61"),sQuery(id+"F0.wireOp",EDGE,"E4.sketch_text.stroke-62"),sQuery(id+"F0.wireOp",EDGE,"E4.sketch_text.stroke-63"),sQuery(id+"F0.wireOp",EDGE,"E4.sketch_text.stroke-64"),sQuery(id+"F0.wireOp",EDGE,"E4.sketch_text.stroke-65"),sQuery(id+"F0.wireOp",EDGE,"E4.sketch_text.stroke-66"),sQuery(id+"F0.wireOp",EDGE,"E4.sketch_text.stroke-67"),sQuery(id+"F0.wireOp",EDGE,"E4.sketch_text.stroke-68"),sQuery(id+"F0.wireOp",EDGE,"E4.sketch_text.stroke-69"),sQuery(id+"F0.wireOp",EDGE,"E4.sketch_text.stroke-70"),sQuery(id+"F0.wireOp",EDGE,"E5.filletArc"),sQuery(id+"F0.wireOp",EDGE,"E6.filletArc"),sQuery(id+"F0.wireOp",EDGE,"E7.filletArc"),sQuery(id+"F0.wireOp",EDGE,"E8.filletArc")])],"isStart":false});var subQ4=makeQuery(id+"F7.imprint","INTERSECT",VERTEX,{"derivedFrom":[makeQuery(id+"F2.opChamfer","BLEND_EDGE",EDGE,{"blendedFrom":[makeQuery(id+"F1.opExtrude","CAP_EDGE",EDGE,{"disambiguationData":[OSD([subQ2])],"isStart":false}),subQ3],"blendedInto":[subQ3]}),subQ0]});Q1=makeQuery(id+"F7.imprint","IMPRINT",FACE,{"disambiguationData":[TD([[makeQuery(id+"F7.imprint","IMPRINT",EDGE,{"disambiguationData":[TD([[subQ4,-1.0]])],"derivedFrom":subQ0}),1.0]])]});}
            var Q2;
            {var subQ0=sQuery(id+"F7.wireOp",EDGE,"E19");var subQ1=sQuery(id+"F0.wireOp",EDGE,"E3");var subQ2=sQuery(id+"F0.wireOp",EDGE,"E2");var subQ3=makeQuery(id+"F1.opExtrude","CAP_FACE",FACE,{"disambiguationData":[OSD([sQuery(id+"F0.wireOp",EDGE,"E0"),sQuery(id+"F0.wireOp",EDGE,"E1"),subQ2,subQ1,sQuery(id+"F0.wireOp",EDGE,"E4.sketch_text.stroke-0"),sQuery(id+"F0.wireOp",EDGE,"E4.sketch_text.stroke-1"),sQuery(id+"F0.wireOp",EDGE,"E4.sketch_text.stroke-2"),sQuery(id+"F0.wireOp",EDGE,"E4.sketch_text.stroke-3"),sQuery(id+"F0.wireOp",EDGE,"E4.sketch_text.stroke-4"),sQuery(id+"F0.wireOp",EDGE,"E4.sketch_text.stroke-5"),sQuery(id+"F0.wireOp",EDGE,"E4.sketch_text.stroke-6"),sQuery(id+"F0.wireOp",EDGE,"E4.sketch_text.stroke-7"),sQuery(id+"F0.wireOp",EDGE,"E4.sketch_text.stroke-8"),sQuery(id+"F0.wireOp",EDGE,"E4.sketch_text.stroke-9"),sQuery(id+"F0.wireOp",EDGE,"E4.sketch_text.stroke-10"),sQuery(id+"F0.wireOp",EDGE,"E4.sketch_text.stroke-11"),sQuery(id+"F0.wireOp",EDGE,"E4.sketch_text.stroke-12"),sQuery(id+"F0.wireOp",EDGE,"E4.sketch_text.stroke-13"),sQuery(id+"F0.wireOp",EDGE,"E4.sketch_text.stroke-14"),sQuery(id+"F0.wireOp",EDGE,"E4.sketch_text.stroke-15"),sQuery(id+"F0.wireOp",EDGE,"E4.sketch_text.stroke-16"),sQuery(id+"F0.wireOp",EDGE,"E4.sketch_text.stroke-17"),sQuery(id+"F0.wireOp",EDGE,"E4.sketch_text.stroke-18"),sQuery(id+"F0.wireOp",EDGE,"E4.sketch_text.stroke-19"),sQuery(id+"F0.wireOp",EDGE,"E4.sketch_text.stroke-20"),sQuery(id+"F0.wireOp",EDGE,"E4.sketch_text.stroke-21"),sQuery(id+"F0.wireOp",EDGE,"E4.sketch_text.stroke-22"),sQuery(id+"F0.wireOp",EDGE,"E4.sketch_text.stroke-23"),sQuery(id+"F0.wireOp",EDGE,"E4.sketch_text.stroke-24"),sQuery(id+"F0.wireOp",EDGE,"E4.sketch_text.stroke-25"),sQuery(id+"F0.wireOp",EDGE,"E4.sketch_text.stroke-26"),sQuery(id+"F0.wireOp",EDGE,"E4.sketch_text.stroke-27"),sQuery(id+"F0.wireOp",EDGE,"E4.sketch_text.stroke-28"),sQuery(id+"F0.wireOp",EDGE,"E4.sketch_text.stroke-29"),sQuery(id+"F0.wireOp",EDGE,"E4.sketch_text.stroke-30"),sQuery(id+"F0.wireOp",EDGE,"E4.sketch_text.stroke-31"),sQuery(id+"F0.wireOp",EDGE,"E4.sketch_text.stroke-32"),sQuery(id+"F0.wireOp",EDGE,"E4.sketch_text.stroke-33"),sQuery(id+"F0.wireOp",EDGE,"E4.sketch_text.stroke-34"),sQuery(id+"F0.wireOp",EDGE,"E4.sketch_text.stroke-35"),sQuery(id+"F0.wireOp",EDGE,"E4.sketch_text.stroke-36"),sQuery(id+"F0.wireOp",EDGE,"E4.sketch_text.stroke-37"),sQuery(id+"F0.wireOp",EDGE,"E4.sketch_text.stroke-38"),sQuery(id+"F0.wireOp",EDGE,"E4.sketch_text.stroke-39"),sQuery(id+"F0.wireOp",EDGE,"E4.sketch_text.stroke-40"),sQuery(id+"F0.wireOp",EDGE,"E4.sketch_text.stroke-41"),sQuery(id+"F0.wireOp",EDGE,"E4.sketch_text.stroke-42"),sQuery(id+"F0.wireOp",EDGE,"E4.sketch_text.stroke-43"),sQuery(id+"F0.wireOp",EDGE,"E4.sketch_text.stroke-44"),sQuery(id+"F0.wireOp",EDGE,"E4.sketch_text.stroke-45"),sQuery(id+"F0.wireOp",EDGE,"E4.sketch_text.stroke-46"),sQuery(id+"F0.wireOp",EDGE,"E4.sketch_text.stroke-47"),sQuery(id+"F0.wireOp",EDGE,"E4.sketch_text.stroke-48"),sQuery(id+"F0.wireOp",EDGE,"E4.sketch_text.stroke-49"),sQuery(id+"F0.wireOp",EDGE,"E4.sketch_text.stroke-50"),sQuery(id+"F0.wireOp",EDGE,"E4.sketch_text.stroke-51"),sQuery(id+"F0.wireOp",EDGE,"E4.sketch_text.stroke-52"),sQuery(id+"F0.wireOp",EDGE,"E4.sketch_text.stroke-53"),sQuery(id+"F0.wireOp",EDGE,"E4.sketch_text.stroke-54"),sQuery(id+"F0.wireOp",EDGE,"E4.sketch_text.stroke-55"),sQuery(id+"F0.wireOp",EDGE,"E4.sketch_text.stroke-56"),sQuery(id+"F0.wireOp",EDGE,"E4.sketch_text.stroke-57"),sQuery(id+"F0.wireOp",EDGE,"E4.sketch_text.stroke-58"),sQuery(id+"F0.wireOp",EDGE,"E4.sketch_text.stroke-59"),sQuery(id+"F0.wireOp",EDGE,"E4.sketch_text.stroke-60"),sQuery(id+"F0.wireOp",EDGE,"E4.sketch_text.stroke-61"),sQuery(id+"F0.wireOp",EDGE,"E4.sketch_text.stroke-62"),sQuery(id+"F0.wireOp",EDGE,"E4.sketch_text.stroke-63"),sQuery(id+"F0.wireOp",EDGE,"E4.sketch_text.stroke-64"),sQuery(id+"F0.wireOp",EDGE,"E4.sketch_text.stroke-65"),sQuery(id+"F0.wireOp",EDGE,"E4.sketch_text.stroke-66"),sQuery(id+"F0.wireOp",EDGE,"E4.sketch_text.stroke-67"),sQuery(id+"F0.wireOp",EDGE,"E4.sketch_text.stroke-68"),sQuery(id+"F0.wireOp",EDGE,"E4.sketch_text.stroke-69"),sQuery(id+"F0.wireOp",EDGE,"E4.sketch_text.stroke-70"),sQuery(id+"F0.wireOp",EDGE,"E5.filletArc"),sQuery(id+"F0.wireOp",EDGE,"E6.filletArc"),sQuery(id+"F0.wireOp",EDGE,"E7.filletArc"),sQuery(id+"F0.wireOp",EDGE,"E8.filletArc")])],"isStart":false});var subQ4=makeQuery(id+"F7.imprint","INTERSECT",VERTEX,{"derivedFrom":[makeQuery(id+"F2.opChamfer","BLEND_EDGE",EDGE,{"blendedFrom":[makeQuery(id+"F1.opExtrude","CAP_EDGE",EDGE,{"disambiguationData":[OSD([subQ2])],"isStart":false}),subQ3],"blendedInto":[subQ3]}),subQ0]});Q2=makeQuery(id+"F7.imprint","IMPRINT",FACE,{"disambiguationData":[TD([[makeQuery(id+"F7.imprint","IMPRINT",EDGE,{"disambiguationData":[TD([[subQ4,-1.0]])],"derivedFrom":subQ0}),1.0]])]});}
            var Q3;
            {var subQ0=sQuery(id+"F7.wireOp",EDGE,"E18");var subQ1=sQuery(id+"F0.wireOp",EDGE,"E2");var subQ2=sQuery(id+"F0.wireOp",EDGE,"E1");var subQ3=makeQuery(id+"F1.opExtrude","CAP_FACE",FACE,{"disambiguationData":[OSD([sQuery(id+"F0.wireOp",EDGE,"E0"),subQ2,subQ1,sQuery(id+"F0.wireOp",EDGE,"E3"),sQuery(id+"F0.wireOp",EDGE,"E4.sketch_text.stroke-0"),sQuery(id+"F0.wireOp",EDGE,"E4.sketch_text.stroke-1"),sQuery(id+"F0.wireOp",EDGE,"E4.sketch_text.stroke-2"),sQuery(id+"F0.wireOp",EDGE,"E4.sketch_text.stroke-3"),sQuery(id+"F0.wireOp",EDGE,"E4.sketch_text.stroke-4"),sQuery(id+"F0.wireOp",EDGE,"E4.sketch_text.stroke-5"),sQuery(id+"F0.wireOp",EDGE,"E4.sketch_text.stroke-6"),sQuery(id+"F0.wireOp",EDGE,"E4.sketch_text.stroke-7"),sQuery(id+"F0.wireOp",EDGE,"E4.sketch_text.stroke-8"),sQuery(id+"F0.wireOp",EDGE,"E4.sketch_text.stroke-9"),sQuery(id+"F0.wireOp",EDGE,"E4.sketch_text.stroke-10"),sQuery(id+"F0.wireOp",EDGE,"E4.sketch_text.stroke-11"),sQuery(id+"F0.wireOp",EDGE,"E4.sketch_text.stroke-12"),sQuery(id+"F0.wireOp",EDGE,"E4.sketch_text.stroke-13"),sQuery(id+"F0.wireOp",EDGE,"E4.sketch_text.stroke-14"),sQuery(id+"F0.wireOp",EDGE,"E4.sketch_text.stroke-15"),sQuery(id+"F0.wireOp",EDGE,"E4.sketch_text.stroke-16"),sQuery(id+"F0.wireOp",EDGE,"E4.sketch_text.stroke-17"),sQuery(id+"F0.wireOp",EDGE,"E4.sketch_text.stroke-18"),sQuery(id+"F0.wireOp",EDGE,"E4.sketch_text.stroke-19"),sQuery(id+"F0.wireOp",EDGE,"E4.sketch_text.stroke-20"),sQuery(id+"F0.wireOp",EDGE,"E4.sketch_text.stroke-21"),sQuery(id+"F0.wireOp",EDGE,"E4.sketch_text.stroke-22"),sQuery(id+"F0.wireOp",EDGE,"E4.sketch_text.stroke-23"),sQuery(id+"F0.wireOp",EDGE,"E4.sketch_text.stroke-24"),sQuery(id+"F0.wireOp",EDGE,"E4.sketch_text.stroke-25"),sQuery(id+"F0.wireOp",EDGE,"E4.sketch_text.stroke-26"),sQuery(id+"F0.wireOp",EDGE,"E4.sketch_text.stroke-27"),sQuery(id+"F0.wireOp",EDGE,"E4.sketch_text.stroke-28"),sQuery(id+"F0.wireOp",EDGE,"E4.sketch_text.stroke-29"),sQuery(id+"F0.wireOp",EDGE,"E4.sketch_text.stroke-30"),sQuery(id+"F0.wireOp",EDGE,"E4.sketch_text.stroke-31"),sQuery(id+"F0.wireOp",EDGE,"E4.sketch_text.stroke-32"),sQuery(id+"F0.wireOp",EDGE,"E4.sketch_text.stroke-33"),sQuery(id+"F0.wireOp",EDGE,"E4.sketch_text.stroke-34"),sQuery(id+"F0.wireOp",EDGE,"E4.sketch_text.stroke-35"),sQuery(id+"F0.wireOp",EDGE,"E4.sketch_text.stroke-36"),sQuery(id+"F0.wireOp",EDGE,"E4.sketch_text.stroke-37"),sQuery(id+"F0.wireOp",EDGE,"E4.sketch_text.stroke-38"),sQuery(id+"F0.wireOp",EDGE,"E4.sketch_text.stroke-39"),sQuery(id+"F0.wireOp",EDGE,"E4.sketch_text.stroke-40"),sQuery(id+"F0.wireOp",EDGE,"E4.sketch_text.stroke-41"),sQuery(id+"F0.wireOp",EDGE,"E4.sketch_text.stroke-42"),sQuery(id+"F0.wireOp",EDGE,"E4.sketch_text.stroke-43"),sQuery(id+"F0.wireOp",EDGE,"E4.sketch_text.stroke-44"),sQuery(id+"F0.wireOp",EDGE,"E4.sketch_text.stroke-45"),sQuery(id+"F0.wireOp",EDGE,"E4.sketch_text.stroke-46"),sQuery(id+"F0.wireOp",EDGE,"E4.sketch_text.stroke-47"),sQuery(id+"F0.wireOp",EDGE,"E4.sketch_text.stroke-48"),sQuery(id+"F0.wireOp",EDGE,"E4.sketch_text.stroke-49"),sQuery(id+"F0.wireOp",EDGE,"E4.sketch_text.stroke-50"),sQuery(id+"F0.wireOp",EDGE,"E4.sketch_text.stroke-51"),sQuery(id+"F0.wireOp",EDGE,"E4.sketch_text.stroke-52"),sQuery(id+"F0.wireOp",EDGE,"E4.sketch_text.stroke-53"),sQuery(id+"F0.wireOp",EDGE,"E4.sketch_text.stroke-54"),sQuery(id+"F0.wireOp",EDGE,"E4.sketch_text.stroke-55"),sQuery(id+"F0.wireOp",EDGE,"E4.sketch_text.stroke-56"),sQuery(id+"F0.wireOp",EDGE,"E4.sketch_text.stroke-57"),sQuery(id+"F0.wireOp",EDGE,"E4.sketch_text.stroke-58"),sQuery(id+"F0.wireOp",EDGE,"E4.sketch_text.stroke-59"),sQuery(id+"F0.wireOp",EDGE,"E4.sketch_text.stroke-60"),sQuery(id+"F0.wireOp",EDGE,"E4.sketch_text.stroke-61"),sQuery(id+"F0.wireOp",EDGE,"E4.sketch_text.stroke-62"),sQuery(id+"F0.wireOp",EDGE,"E4.sketch_text.stroke-63"),sQuery(id+"F0.wireOp",EDGE,"E4.sketch_text.stroke-64"),sQuery(id+"F0.wireOp",EDGE,"E4.sketch_text.stroke-65"),sQuery(id+"F0.wireOp",EDGE,"E4.sketch_text.stroke-66"),sQuery(id+"F0.wireOp",EDGE,"E4.sketch_text.stroke-67"),sQuery(id+"F0.wireOp",EDGE,"E4.sketch_text.stroke-68"),sQuery(id+"F0.wireOp",EDGE,"E4.sketch_text.stroke-69"),sQuery(id+"F0.wireOp",EDGE,"E4.sketch_text.stroke-70"),sQuery(id+"F0.wireOp",EDGE,"E5.filletArc"),sQuery(id+"F0.wireOp",EDGE,"E6.filletArc"),sQuery(id+"F0.wireOp",EDGE,"E7.filletArc"),sQuery(id+"F0.wireOp",EDGE,"E8.filletArc")])],"isStart":false});var subQ4=makeQuery(id+"F7.imprint","INTERSECT",VERTEX,{"derivedFrom":[makeQuery(id+"F2.opChamfer","BLEND_EDGE",EDGE,{"blendedFrom":[makeQuery(id+"F1.opExtrude","CAP_EDGE",EDGE,{"disambiguationData":[OSD([subQ2])],"isStart":false}),subQ3],"blendedInto":[subQ3]}),subQ0]});Q3=makeQuery(id+"F7.imprint","IMPRINT",FACE,{"disambiguationData":[TD([[makeQuery(id+"F7.imprint","IMPRINT",EDGE,{"disambiguationData":[TD([[subQ4,1.0]])],"derivedFrom":subQ0}),1.0]])]});}
            extrude(context, id + "F8", {"entities" : qUnion([Q0, Q1, Q2, Q3]), "operationType" : NewBodyOperationType.ADD, "depth" : 9 * mm});
        }
        {
            var Q0;
            Q0=makeQuery(id+"F5.opExtrude","CAP_FACE",FACE,{"disambiguationData":[OSD([sQuery(id+"F4.wireOp",EDGE,"E9.bottom"),sQuery(id+"F4.wireOp",EDGE,"E9.top"),sQuery(id+"F4.wireOp",EDGE,"E9.left"),sQuery(id+"F4.wireOp",EDGE,"E9.right"),sQuery(id+"F4.wireOp",EDGE,"E13.filletArc"),sQuery(id+"F4.wireOp",EDGE,"E14.filletArc"),sQuery(id+"F4.wireOp",EDGE,"E15.filletArc"),sQuery(id+"F4.wireOp",EDGE,"E16.filletArc"),sQuery(id+"F4.wireOp",EDGE,"E17.bottom"),sQuery(id+"F4.wireOp",EDGE,"E17.top"),sQuery(id+"F4.wireOp",EDGE,"E17.left"),sQuery(id+"F4.wireOp",EDGE,"E17.right")])],"isStart":false});
            var sketch = newSketch(context, id + "F9", { "sketchPlane" : qUnion([Q0])});
            skCircle(sketch, "E22", {"center": v(-59, 29) * mm, "radius": 2 * mm});
            skCircle(sketch, "E23", {"center": v(-57, -7) * mm, "radius": 2 * mm});
            skCircle(sketch, "E24", {"center": v(57, -7) * mm, "radius": 2 * mm});
            skCircle(sketch, "E25", {"center": v(57, 27) * mm, "radius": 2 * mm});
            skSolve(sketch);
        }
        {
            var Q0;
            Q0=makeQuery(id+"F9.imprint","IMPRINT",FACE,{"disambiguationData":[TD([[makeQuery(id+"F9.imprint","IMPRINT",EDGE,{"derivedFrom":sQuery(id+"F9.wireOp",EDGE,"E22")}),1.0]])]});
            var Q1;
            Q1=makeQuery(id+"F9.imprint","IMPRINT",FACE,{"disambiguationData":[TD([[makeQuery(id+"F9.imprint","IMPRINT",EDGE,{"derivedFrom":sQuery(id+"F9.wireOp",EDGE,"E23")}),1.0]])]});
            var Q2;
            Q2=makeQuery(id+"F9.imprint","IMPRINT",FACE,{"disambiguationData":[TD([[makeQuery(id+"F9.imprint","IMPRINT",EDGE,{"derivedFrom":sQuery(id+"F9.wireOp",EDGE,"E24")}),1.0]])]});
            var Q3;
            Q3=makeQuery(id+"F9.imprint","IMPRINT",FACE,{"disambiguationData":[TD([[makeQuery(id+"F9.imprint","IMPRINT",EDGE,{"derivedFrom":sQuery(id+"F9.wireOp",EDGE,"E25")}),1.0]])]});
            extrude(context, id + "F10", {"entities" : qUnion([Q0, Q1, Q2, Q3]), "operationType" : NewBodyOperationType.ADD, "depth" : 10 * mm});
        }
        {
            var Q0;
            Q0=makeQuery(id+"F10.opExtrude","CAP_FACE",FACE,{"disambiguationData":[OSD([sQuery(id+"F9.wireOp",EDGE,"E22")])],"isStart":false});
            var sketch = newSketch(context, id + "F11", { "sketchPlane" : qUnion([Q0])});
            skLineSegment(sketch, "E26", {"start": v(-60.41, 27.59) * mm, "end": v(-48.41, 15.59) * mm});
            skLineSegment(sketch, "E27", {"start": v(-57.59, 30.41) * mm, "end": v(-45.59, 18.41) * mm});
            skLineSegment(sketch, "E28", {"start": v(-57.59, 30.41) * mm, "end": v(-60.41, 27.59) * mm});
            skLineSegment(sketch, "E29", {"start": v(-45.59, 18.41) * mm, "end": v(-48.41, 15.59) * mm});
            skLineSegment(sketch, "E30.MirrorCS", {"start": v(-45.59, 1.59) * mm, "end": v(-48.41, 4.41) * mm});
            skLineSegment(sketch, "E31.MirrorCS", {"start": v(-55.59, -8.41) * mm, "end": v(-58.41, -5.59) * mm});
            skLineSegment(sketch, "E32.MirrorCS", {"start": v(-58.41, -5.59) * mm, "end": v(-48.41, 4.41) * mm});
            skLineSegment(sketch, "E33.MirrorCS", {"start": v(-55.59, -8.41) * mm, "end": v(-45.59, 1.59) * mm});
            skLineSegment(sketch, "E34", {"start": v(55.59, -8.41) * mm, "end": v(45.59, 1.59) * mm});
            skLineSegment(sketch, "E35", {"start": v(45.59, 1.59) * mm, "end": v(48.41, 4.41) * mm});
            skLineSegment(sketch, "E36", {"start": v(48.41, 4.41) * mm, "end": v(58.41, -5.59) * mm});
            skLineSegment(sketch, "E37", {"start": v(58.41, -5.59) * mm, "end": v(55.59, -8.41) * mm});
            skLineSegment(sketch, "E38", {"start": v(48.41, 15.59) * mm, "end": v(58.41, 25.59) * mm});
            skLineSegment(sketch, "E39", {"start": v(58.41, 25.59) * mm, "end": v(55.59, 28.41) * mm});
            skLineSegment(sketch, "E40", {"start": v(55.59, 28.41) * mm, "end": v(45.59, 18.41) * mm});
            skLineSegment(sketch, "E41", {"start": v(45.59, 18.41) * mm, "end": v(48.41, 15.59) * mm});
            skSolve(sketch);
        }
        {
            var Q0;
            {var subQ0=sQuery(id+"F11.wireOp",EDGE,"E26");Q0=makeQuery(id+"F11.imprint","IMPRINT",FACE,{"disambiguationData":[TD([[makeQuery(id+"F11.imprint","IMPRINT",EDGE,{"derivedFrom":subQ0}),1.0]])]});}
            var Q1;
            {var subQ0=sQuery(id+"F11.wireOp",EDGE,"E28");Q1=makeQuery(id+"F11.imprint","IMPRINT",FACE,{"disambiguationData":[TD([[makeQuery(id+"F11.imprint","IMPRINT",EDGE,{"derivedFrom":subQ0}),1.0]])]});}
            var Q2;
            Q2=makeQuery(id+"F10.opExtrude","CAP_FACE",FACE,{"disambiguationData":[OSD([sQuery(id+"F9.wireOp",EDGE,"E23")])],"isStart":false});
            var Q3;
            Q3=makeQuery(id+"F11.imprint","IMPRINT",FACE,{"disambiguationData":[TD([[makeQuery(id+"F11.imprint","IMPRINT",EDGE,{"derivedFrom":sQuery(id+"F11.wireOp",EDGE,"E30.MirrorCS")}),1.0]])]});
            var Q4;
            Q4=makeQuery(id+"F8.opExtrude","CAP_FACE",FACE,{"disambiguationData":[OSD([sQuery(id+"F7.wireOp",EDGE,"E21")])],"isStart":false});
            var Q5;
            Q5=makeQuery(id+"F8.opExtrude","CAP_FACE",FACE,{"disambiguationData":[OSD([sQuery(id+"F7.wireOp",EDGE,"E20")])],"isStart":false});
            var Q6;
            {var subQ0=sQuery(id+"F11.wireOp",EDGE,"E28");Q6=makeQuery(id+"F11.imprint","IMPRINT",FACE,{"disambiguationData":[TD([[makeQuery(id+"F11.imprint","IMPRINT",EDGE,{"derivedFrom":subQ0}),-1.0]])]});}
            var Q7;
            Q7=makeQuery(id+"F11.imprint","IMPRINT",FACE,{"disambiguationData":[TD([[makeQuery(id+"F11.imprint","IMPRINT",EDGE,{"derivedFrom":sQuery(id+"F11.wireOp",EDGE,"E38")}),1.0]])]});
            var Q8;
            Q8=makeQuery(id+"F10.opExtrude","CAP_FACE",FACE,{"disambiguationData":[OSD([sQuery(id+"F9.wireOp",EDGE,"E25")])],"isStart":false});
            var Q9;
            Q9=makeQuery(id+"F8.opExtrude","CAP_FACE",FACE,{"disambiguationData":[OSD([sQuery(id+"F7.wireOp",EDGE,"E19")])],"isStart":false});
            var Q10;
            Q10=makeQuery(id+"F11.imprint","IMPRINT",FACE,{"disambiguationData":[TD([[makeQuery(id+"F11.imprint","IMPRINT",EDGE,{"derivedFrom":sQuery(id+"F11.wireOp",EDGE,"E34")}),-1.0]])]});
            var Q11;
            Q11=makeQuery(id+"F10.opExtrude","CAP_FACE",FACE,{"disambiguationData":[OSD([sQuery(id+"F9.wireOp",EDGE,"E24")])],"isStart":false});
            var Q12;
            Q12=makeQuery(id+"F8.opExtrude","CAP_FACE",FACE,{"disambiguationData":[OSD([sQuery(id+"F7.wireOp",EDGE,"E18")])],"isStart":false});
            extrude(context, id + "F12", {"entities" : qUnion([Q0, Q1, Q2, Q3, Q4, Q5, Q6, Q7, Q8, Q9, Q10, Q11, Q12]), "depth" : 4 * mm});
        }
        {
            var Q0;
            Q0=makeQuery(id+"F12.opExtrude","CAP_EDGE",EDGE,{"disambiguationData":[OSD([sQuery(id+"F7.wireOp",EDGE,"E20")])],"isStart":false});
            var Q1;
            Q1=makeQuery(id+"F12.opExtrude","CAP_EDGE",EDGE,{"disambiguationData":[OSD([sQuery(id+"F11.wireOp",EDGE,"E33.MirrorCS")])],"isStart":false});
            var Q2;
            Q2=makeQuery(id+"F12.opExtrude","CAP_EDGE",EDGE,{"disambiguationData":[OSD([sQuery(id+"F7.wireOp",EDGE,"E21")])],"isStart":false});
            var Q3;
            Q3=makeQuery(id+"F12.opExtrude","CAP_EDGE",EDGE,{"disambiguationData":[OSD([sQuery(id+"F9.wireOp",EDGE,"E23")])],"isStart":false});
            var Q4;
            Q4=makeQuery(id+"F12.opExtrude","CAP_EDGE",EDGE,{"disambiguationData":[OSD([sQuery(id+"F11.wireOp",EDGE,"E32.MirrorCS")])],"isStart":false});
            var Q5;
            Q5=makeQuery(id+"F12.opExtrude","CAP_EDGE",EDGE,{"disambiguationData":[OSD([sQuery(id+"F11.wireOp",EDGE,"E34")])],"isStart":false});
            var Q6;
            Q6=makeQuery(id+"F12.opExtrude","CAP_EDGE",EDGE,{"disambiguationData":[OSD([sQuery(id+"F7.wireOp",EDGE,"E19")])],"isStart":false});
            var Q7;
            Q7=makeQuery(id+"F12.opExtrude","CAP_EDGE",EDGE,{"disambiguationData":[OSD([sQuery(id+"F9.wireOp",EDGE,"E24")])],"isStart":false});
            var Q8;
            Q8=makeQuery(id+"F12.opExtrude","CAP_EDGE",EDGE,{"disambiguationData":[OSD([sQuery(id+"F11.wireOp",EDGE,"E36")])],"isStart":false});
            var Q9;
            Q9=makeQuery(id+"F12.opExtrude","CAP_EDGE",EDGE,{"disambiguationData":[OSD([sQuery(id+"F9.wireOp",EDGE,"E25")])],"isStart":false});
            var Q10;
            Q10=makeQuery(id+"F12.opExtrude","CAP_EDGE",EDGE,{"disambiguationData":[OSD([sQuery(id+"F11.wireOp",EDGE,"E38")])],"isStart":false});
            var Q11;
            Q11=makeQuery(id+"F12.opExtrude","CAP_EDGE",EDGE,{"disambiguationData":[OSD([sQuery(id+"F11.wireOp",EDGE,"E40")])],"isStart":false});
            var Q12;
            Q12=makeQuery(id+"F12.opExtrude","CAP_EDGE",EDGE,{"disambiguationData":[OSD([sQuery(id+"F7.wireOp",EDGE,"E18")])],"isStart":false});
            var Q13;
            Q13=makeQuery(id+"F12.opExtrude","CAP_EDGE",EDGE,{"disambiguationData":[OSD([sQuery(id+"F11.wireOp",EDGE,"E26")])],"isStart":false});
            var Q14;
            Q14=makeQuery(id+"F12.opExtrude","CAP_EDGE",EDGE,{"disambiguationData":[OSD([sQuery(id+"F11.wireOp",EDGE,"E27")])],"isStart":false});
            fillet(context, id + "F13", {"entities" : qUnion([Q0, Q1, Q2, Q3, Q4, Q5, Q6, Q7, Q8, Q9, Q10, Q11, Q12, Q13, Q14]), "radius" : 2 * mm, "tangentPropagation" : true, "allowEdgeOverflow" : false});
        }
    });
